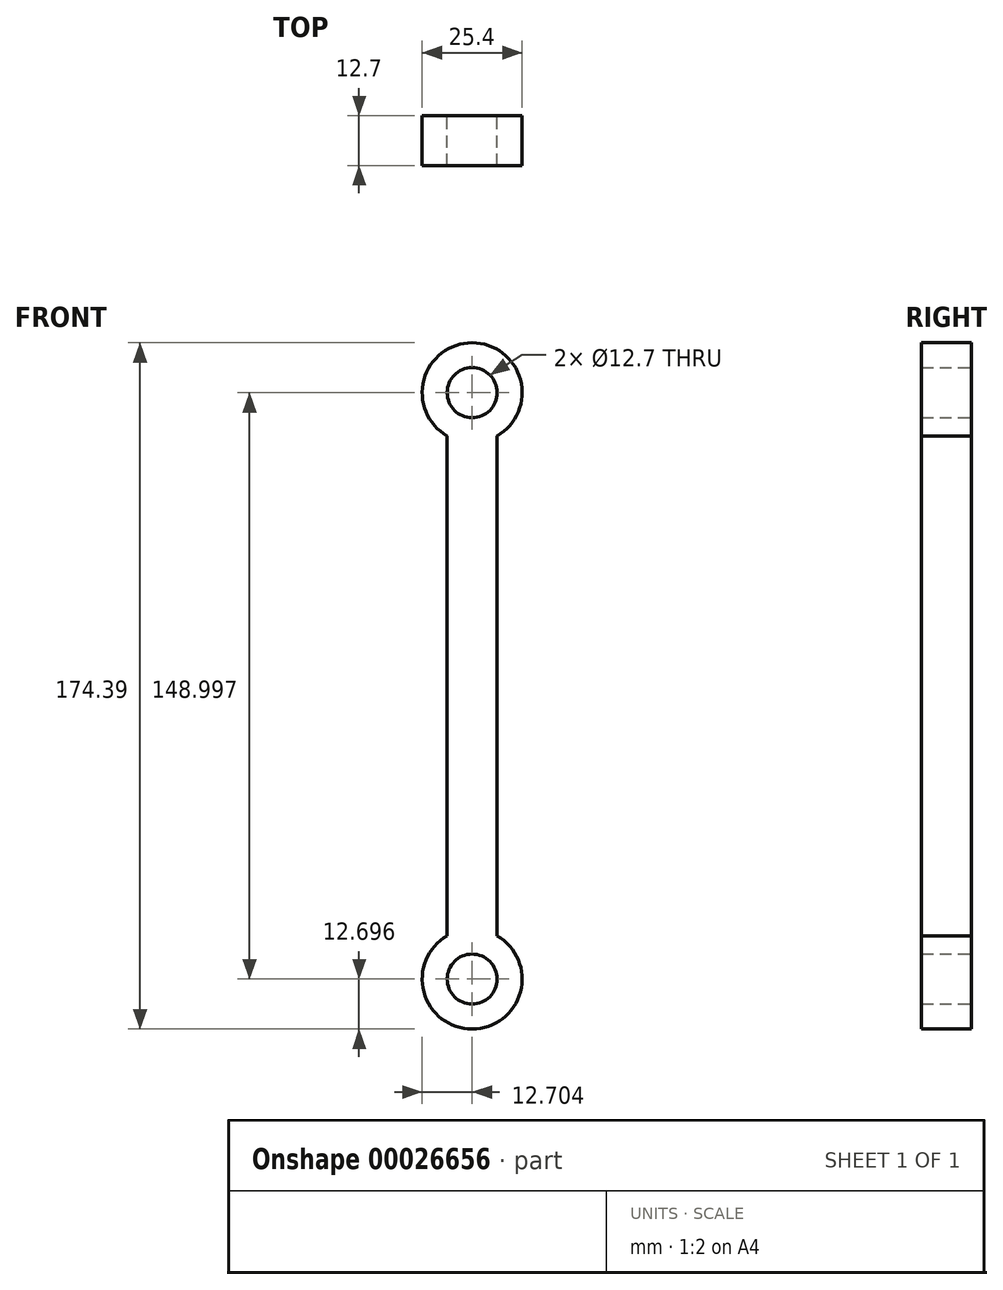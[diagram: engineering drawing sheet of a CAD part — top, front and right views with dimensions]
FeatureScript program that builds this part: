
annotation { "Feature Type Name" : "Feature", "Feature Type Description" : "" }
export const myFeature = defineFeature(function(context is Context, id is Id, definition is map)
    precondition{}
    {
        {
            var Q0;
            Q0=qCreatedBy(makeId("Front.planeOp"),FACE);
            var sketch = newSketch(context, id + "F0", { "sketchPlane" : qUnion([Q0])});
            skCircle(sketch, "E0", {"center": v(-13.98, -71.61) * mm, "radius": 12.7 * mm});
            skCircle(sketch, "E1", {"center": v(-13.98, -71.61) * mm, "radius": 6.35 * mm});
            skLineSegment(sketch, "E2", {"start": v(-20.33, -60.62) * mm, "end": v(-20.33, 66.38) * mm});
            skLineSegment(sketch, "E3", {"start": v(-7.63, -60.62) * mm, "end": v(-7.63, 66.38) * mm});
            skLineSegment(sketch, "E4", {"start": v(-20.33, 66.38) * mm, "end": v(-7.63, 66.38) * mm});
            skLineSegment(sketch, "E5", {"start": v(-13.98, 66.38) * mm, "end": v(-13.98, 77.38) * mm});
            skCircle(sketch, "E6", {"center": v(-13.98, 77.38) * mm, "radius": 12.7 * mm});
            skCircle(sketch, "E7", {"center": v(-13.98, 77.38) * mm, "radius": 6.35 * mm});
            skSolve(sketch);
        }
        {
            var Q0;
            Q0 = qSketchRegion(id + "F0", true);
            extrude(context, id + "F1", {"entities" : qUnion([Q0]), "depth" : 12.7 * mm});
        }
    });
